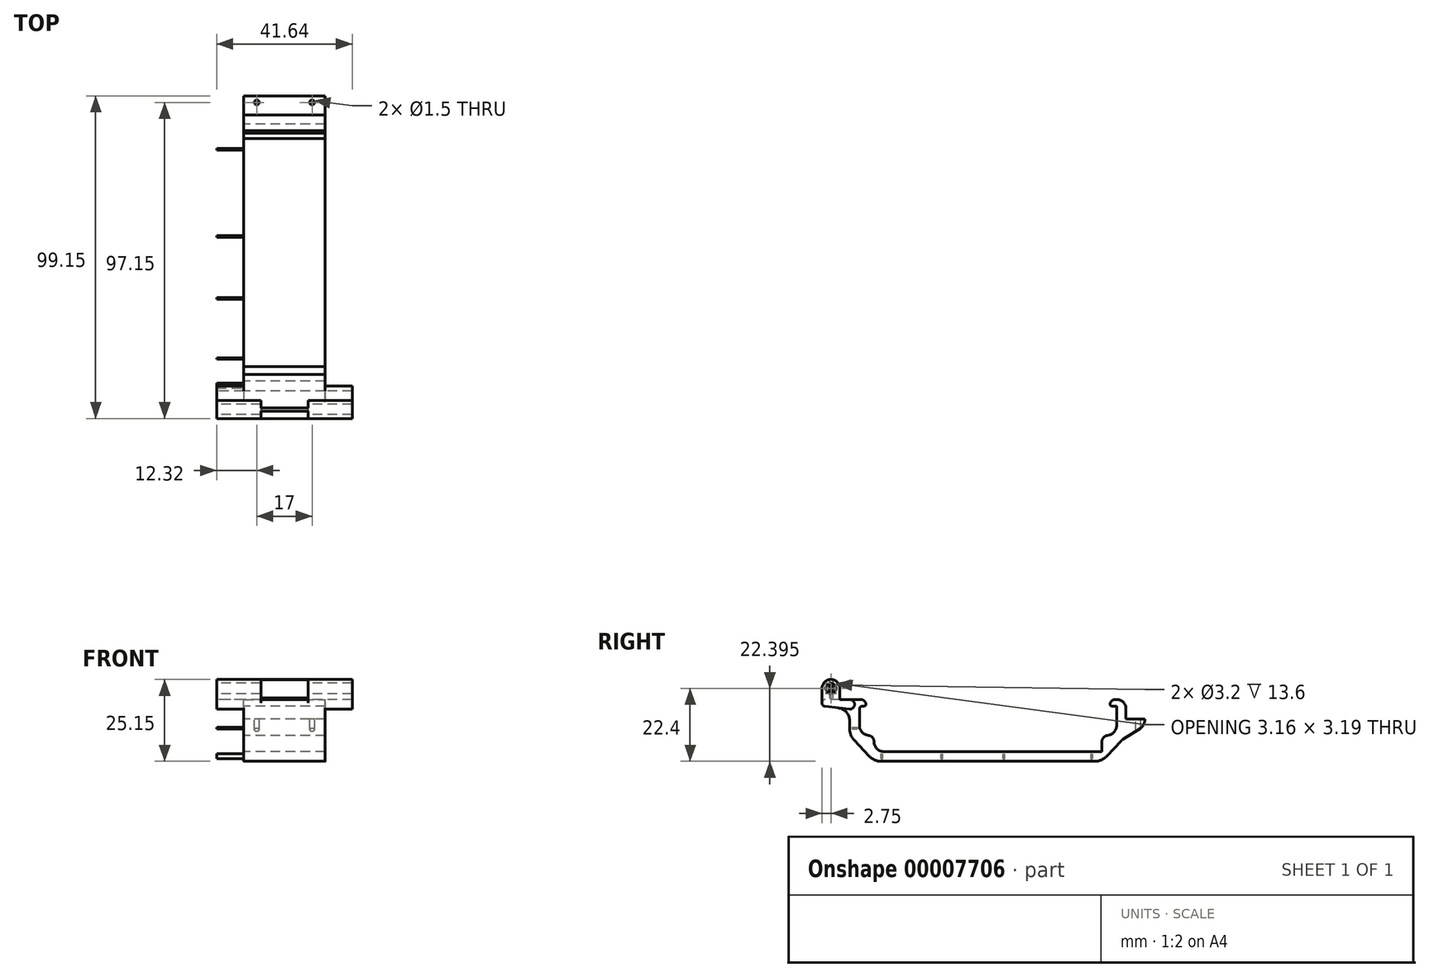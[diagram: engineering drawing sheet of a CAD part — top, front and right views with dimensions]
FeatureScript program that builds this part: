
annotation { "Feature Type Name" : "Feature", "Feature Type Description" : "" }
export const myFeature = defineFeature(function(context is Context, id is Id, definition is map)
    precondition{}
    {
        {
            var Q0;
            Q0=qCreatedBy(makeId("Right.planeOp"),FACE);
            var sketch = newSketch(context, id + "F0", { "sketchPlane" : qUnion([Q0])});
            skLineSegment(sketch, "E0.bottom", {"start": v(-38.5, 0) * mm, "end": v(-38, 0) * mm});
            skLineSegment(sketch, "E0.left", {"start": v(-39.5, -1) * mm, "end": v(-39.5, -6) * mm});
            skLineSegment(sketch, "E0.right", {"start": v(39.5, 0) * mm, "end": v(39.5, -9) * mm});
            skLineSegment(sketch, "E1.bottom", {"start": v(-35, -9) * mm, "end": v(35, -9) * mm});
            skLineSegment(sketch, "E1.top", {"start": v(-32, -14) * mm, "end": v(35, -14) * mm});
            skLineSegment(sketch, "E1.left", {"start": v(-35, -11) * mm, "end": v(-35, -11) * mm});
            skLineSegment(sketch, "E1.right", {"start": v(35, -9) * mm, "end": v(35, -14) * mm});
            skLineSegment(sketch, "E2", {"start": v(0, -14) * mm, "end": v(0, 0) * mm, "construction": true});
            skLineSegment(sketch, "E3.0", {"start": v(-42.5, -1) * mm, "end": v(-42.5, -7.02) * mm});
            skLineSegment(sketch, "E4.0", {"start": v(-32.83, -17) * mm, "end": v(0, -17) * mm});
            skLineSegment(sketch, "E5", {"start": v(-41.15, -10.44) * mm, "end": v(-36.48, -15.42) * mm});
            skLineSegment(sketch, "E6", {"start": v(-37.5, 0.5) * mm, "end": v(-37.5, 2) * mm});
            skLineSegment(sketch, "E7", {"start": v(-37.5, 2) * mm, "end": v(-39.5, 2) * mm});
            skPoint(sketch, "E8.visualSharp", {"position": v(-39.5, 0) * mm});
            skArc(sketch, "E8.filletArc", {"start": v(-38.5, 0) * mm, "mid": v(-39.2, -0.3) * mm, "end": v(-39.5, -1) * mm});
            skPoint(sketch, "E9.visualSharp", {"position": v(-39.5, -9) * mm});
            skArc(sketch, "E9.filletArc", {"start": v(-39.5, -6) * mm, "mid": v(-38.62, -8.12) * mm, "end": v(-36.5, -9) * mm});
            skArc(sketch, "E10.filletArc", {"start": v(-35, -11) * mm, "mid": v(-35.59, -9.59) * mm, "end": v(-37, -9) * mm});
            skPoint(sketch, "E11.visualSharp", {"position": v(-35, -14) * mm});
            skArc(sketch, "E11.filletArc", {"start": v(-35, -11) * mm, "mid": v(-34.12, -13.12) * mm, "end": v(-32, -14) * mm});
            skPoint(sketch, "E12.visualSharp", {"position": v(-42.5, -9) * mm});
            skArc(sketch, "E12.filletArc", {"start": v(-42.5, -7.02) * mm, "mid": v(-42.15, -8.86) * mm, "end": v(-41.15, -10.44) * mm});
            skPoint(sketch, "E13.visualSharp", {"position": v(-35, -17) * mm});
            skArc(sketch, "E13.filletArc", {"start": v(-36.48, -15.42) * mm, "mid": v(-34.82, -16.59) * mm, "end": v(-32.83, -17) * mm});
            skPoint(sketch, "E14.visualSharp", {"position": v(-42.5, 2) * mm});
            skArc(sketch, "E14.filletArc", {"start": v(-39.5, 2) * mm, "mid": v(-41.62, 1.12) * mm, "end": v(-42.5, -1) * mm});
            skPoint(sketch, "E15.newPointA", {"position": v(39.5, 0) * mm});
            skPoint(sketch, "E15.newPointB", {"position": v(-37.5, 0) * mm});
            skArc(sketch, "E15.filletArc", {"start": v(-38, 0) * mm, "mid": v(-37.65, 0.15) * mm, "end": v(-37.5, 0.5) * mm});
            skLineSegment(sketch, "E16.MirrorCS", {"start": v(37.5, 2) * mm, "end": v(39.5, 2) * mm});
            skLineSegment(sketch, "E17.MirrorCS", {"start": v(37.5, 0.5) * mm, "end": v(37.5, 2) * mm});
            skArc(sketch, "E18.MirrorCS", {"start": v(38, 0) * mm, "mid": v(37.65, 0.15) * mm, "end": v(37.5, 0.5) * mm});
            skLineSegment(sketch, "E19.MirrorCS", {"start": v(38.5, 0) * mm, "end": v(38, 0) * mm});
            skArc(sketch, "E20.MirrorCS", {"start": v(38.5, 0) * mm, "mid": v(39.2, -0.3) * mm, "end": v(39.5, -1) * mm});
            skLineSegment(sketch, "E21.MirrorCS", {"start": v(39.5, -1) * mm, "end": v(39.5, -6) * mm});
            skArc(sketch, "E22.MirrorCS", {"start": v(39.5, 2) * mm, "mid": v(41.62, 1.12) * mm, "end": v(42.5, -1) * mm});
            skLineSegment(sketch, "E23.MirrorCS", {"start": v(42.5, -1) * mm, "end": v(42.5, -7.02) * mm});
            skArc(sketch, "E24.MirrorCS", {"start": v(42.5, -7.02) * mm, "mid": v(42.15, -8.86) * mm, "end": v(41.15, -10.44) * mm});
            skLineSegment(sketch, "E25.MirrorCS", {"start": v(41.15, -10.44) * mm, "end": v(36.48, -15.42) * mm});
            skArc(sketch, "E26.MirrorCS", {"start": v(36.48, -15.42) * mm, "mid": v(34.82, -16.59) * mm, "end": v(32.83, -17) * mm});
            skLineSegment(sketch, "E27.MirrorCS", {"start": v(32.83, -17) * mm, "end": v(0, -17) * mm});
            skArc(sketch, "E28.MirrorCS", {"start": v(35, -11) * mm, "mid": v(34.12, -13.12) * mm, "end": v(32, -14) * mm});
            skArc(sketch, "E29.MirrorCS", {"start": v(35, -11) * mm, "mid": v(35.59, -9.59) * mm, "end": v(37, -9) * mm});
            skArc(sketch, "E30.MirrorCS", {"start": v(39.5, -6) * mm, "mid": v(38.62, -8.12) * mm, "end": v(36.5, -9) * mm});
            skLineSegment(sketch, "E31", {"start": v(36.68, -9.03) * mm, "end": v(37.1, -8.94) * mm});
            skLineSegment(sketch, "E32", {"start": v(-36.61, -9.04) * mm, "end": v(-37.1, -8.94) * mm});
            skLineSegment(sketch, "E33", {"start": v(51, 0) * mm, "end": v(-51, 0) * mm});
            skLineSegment(sketch, "E34.0", {"start": v(51, 2.65) * mm, "end": v(-51, 2.65) * mm});
            skCircle(sketch, "E35", {"center": v(-48.25, 2.75) * mm, "radius": 2.65 * mm, "construction": true});
            skLineSegment(sketch, "E36.bottom", {"start": v(44.15, 3) * mm, "end": v(48.15, 3) * mm});
            skLineSegment(sketch, "E36.top", {"start": v(44.15, 0) * mm, "end": v(48.15, 0) * mm});
            skLineSegment(sketch, "E36.left", {"start": v(44.15, 3) * mm, "end": v(44.15, 0) * mm});
            skLineSegment(sketch, "E36.right", {"start": v(48.15, 3) * mm, "end": v(48.15, 0) * mm});
            skLineSegment(sketch, "E37", {"start": v(51, 2.65) * mm, "end": v(51, 0) * mm});
            skLineSegment(sketch, "E38", {"start": v(-51, 0) * mm, "end": v(-42.5, -1) * mm});
            skLineSegment(sketch, "E39", {"start": v(-39.5, 2) * mm, "end": v(-53.6, 2) * mm});
            skLineSegment(sketch, "E40", {"start": v(39.5, 2) * mm, "end": v(44.15, 2) * mm});
            skCircle(sketch, "E41", {"center": v(-48.35, 2.65) * mm, "radius": 1.45 * mm, "construction": true});
            skLineSegment(sketch, "E42", {"start": v(-42.5, 2) * mm, "end": v(-42.5, -1) * mm, "construction": true});
            skArc(sketch, "E43", {"start": v(-42.85, -0.96) * mm, "mid": v(-41.5, 1.62) * mm, "end": v(-43.91, 0) * mm});
            skLineSegment(sketch, "E44", {"start": v(44.15, 2) * mm, "end": v(51, 2) * mm});
            skLineSegment(sketch, "E45", {"start": v(48.15, 0) * mm, "end": v(48.15, -6) * mm});
            skCircle(sketch, "E46", {"center": v(-48.25, 5.4) * mm, "radius": 2.75 * mm});
            skCircle(sketch, "E47", {"center": v(-48.25, 5.4) * mm, "radius": 1.6 * mm});
            skLineSegment(sketch, "E48", {"start": v(-51, 0) * mm, "end": v(-51, 5.4) * mm});
            skLineSegment(sketch, "E49", {"start": v(-45.5, 2) * mm, "end": v(-45.5, 5.4) * mm});
            skLineSegment(sketch, "E50", {"start": v(44.15, 0) * mm, "end": v(44.15, -8.54) * mm});
            skLineSegment(sketch, "E51", {"start": v(41.15, -10.44) * mm, "end": v(48.15, -6) * mm});
            skSolve(sketch);
        }
        {
            var Q0;
            {var subQ8=sQuery(id+"F0.wireOp",EDGE,"E0.left");Q0=makeQuery(id+"F0.imprint","IMPRINT",FACE,{"disambiguationData":[TD([[makeQuery(id+"F0.imprint","IMPRINT",EDGE,{"derivedFrom":subQ8}),-1.0]])]});}
            var Q1;
            {var subQ3=sQuery(id+"F0.wireOp",EDGE,"E16.MirrorCS");Q1=makeQuery(id+"F0.imprint","IMPRINT",FACE,{"disambiguationData":[TD([[makeQuery(id+"F0.imprint","IMPRINT",EDGE,{"derivedFrom":subQ3}),-1.0]])]});}
            var Q2;
            {var subQ4=sQuery(id+"F0.wireOp",EDGE,"E0.bottom");Q2=makeQuery(id+"F0.imprint","IMPRINT",FACE,{"disambiguationData":[TD([[makeQuery(id+"F0.imprint","IMPRINT",EDGE,{"derivedFrom":subQ4}),1.0]])]});}
            var Q3;
            {var subQ0=sQuery(id+"F0.wireOp",EDGE,"E43");var subQ1=sQuery(id+"F0.wireOp",EDGE,"E14.filletArc");var subQ2=makeQuery(id+"F0.imprint","INTERSECT",VERTEX,{"derivedFrom":[subQ1,subQ0]});Q3=makeQuery(id+"F0.imprint","IMPRINT",FACE,{"disambiguationData":[TD([[makeQuery(id+"F0.imprint","IMPRINT",EDGE,{"disambiguationData":[TD([[subQ2,-1.0]])],"derivedFrom":subQ1}),1.0]])]});}
            var Q4;
            {var subQ1=sQuery(id+"F0.wireOp",EDGE,"E14.filletArc");var subQ3=sQuery(id+"F0.wireOp",EDGE,"E33");var subQ4=makeQuery(id+"F0.imprint","INTERSECT",VERTEX,{"derivedFrom":[subQ1,subQ3]});Q4=makeQuery(id+"F0.imprint","IMPRINT",FACE,{"disambiguationData":[TD([[makeQuery(id+"F0.imprint","IMPRINT",EDGE,{"disambiguationData":[TD([[subQ4,1.0]])],"derivedFrom":subQ3}),1.0]])]});}
            var Q5;
            {var subQ0=sQuery(id+"F0.wireOp",EDGE,"E39");var subQ3=sQuery(id+"F0.wireOp",EDGE,"E43");var subQ5=makeQuery(id+"F0.imprint","INTERSECT",VERTEX,{"derivedFrom":[subQ0,subQ3]});Q5=makeQuery(id+"F0.imprint","IMPRINT",FACE,{"disambiguationData":[TD([[makeQuery(id+"F0.imprint","IMPRINT",EDGE,{"disambiguationData":[TD([[subQ5,1.0]])],"derivedFrom":subQ3}),-1.0]])]});}
            var Q6;
            {var subQ0=sQuery(id+"F0.wireOp",EDGE,"E43");var subQ1=sQuery(id+"F0.wireOp",EDGE,"E14.filletArc");var subQ2=makeQuery(id+"F0.imprint","INTERSECT",VERTEX,{"derivedFrom":[subQ1,subQ0]});Q6=makeQuery(id+"F0.imprint","IMPRINT",FACE,{"disambiguationData":[TD([[makeQuery(id+"F0.imprint","IMPRINT",EDGE,{"disambiguationData":[TD([[subQ2,-1.0]])],"derivedFrom":subQ1}),-1.0]])]});}
            var Q7;
            {var subQ3=sQuery(id+"F0.wireOp",EDGE,"E43");var subQ5=sQuery(id+"F0.wireOp",EDGE,"E33");var subQ6=makeQuery(id+"F0.imprint","INTERSECT",VERTEX,{"disambiguationData":[OD(0.0)],"derivedFrom":[subQ5,subQ3]});Q7=makeQuery(id+"F0.imprint","IMPRINT",FACE,{"disambiguationData":[TD([[makeQuery(id+"F0.imprint","IMPRINT",EDGE,{"disambiguationData":[TD([[subQ6,-1.0]])],"derivedFrom":subQ5}),1.0]])]});}
            var Q8;
            {var subQ4=sQuery(id+"F0.wireOp",EDGE,"ue2dPaGK-Ie0L-X2Up-9sbi-YMYjDMFNOoKe");Q8=makeQuery(id+"F0.imprint","IMPRINT",FACE,{"disambiguationData":[TD([[makeQuery(id+"F0.imprint","IMPRINT",EDGE,{"derivedFrom":subQ4}),1.0]])]});}
            var Q9;
            {var subQ0=sQuery(id+"F0.wireOp",EDGE,"E20.MirrorCS");Q9=makeQuery(id+"F0.imprint","IMPRINT",FACE,{"disambiguationData":[TD([[makeQuery(id+"F0.imprint","IMPRINT",EDGE,{"derivedFrom":subQ0}),1.0]])]});}
            var Q10;
            {var subQ4=sQuery(id+"F0.wireOp",EDGE,"E45");Q10=makeQuery(id+"F0.imprint","IMPRINT",FACE,{"disambiguationData":[TD([[makeQuery(id+"F0.imprint","IMPRINT",EDGE,{"derivedFrom":subQ4}),-1.0]])]});}
            var Q11;
            {var subQ3=sQuery(id+"F0.wireOp",EDGE,"E28.MirrorCS");Q11=makeQuery(id+"F0.imprint","IMPRINT",FACE,{"disambiguationData":[TD([[makeQuery(id+"F0.imprint","IMPRINT",EDGE,{"derivedFrom":subQ3}),1.0]])]});}
            var Q12;
            {var subQ3=sQuery(id+"F0.wireOp",EDGE,"E39");var subQ8=makeQuery(id+"F0.imprint","INTERSECT",VERTEX,{"derivedFrom":[subQ3,sQuery(id+"F0.wireOp",EDGE,"E49")]});Q12=makeQuery(id+"F0.imprint","IMPRINT",FACE,{"disambiguationData":[TD([[makeQuery(id+"F0.imprint","IMPRINT",EDGE,{"disambiguationData":[TD([[subQ8,-1.0]])],"derivedFrom":subQ3}),1.0]])]});}
            var Q13;
            {var subQ5=sQuery(id+"F0.wireOp",EDGE,"E23.MirrorCS");Q13=makeQuery(id+"F0.imprint","IMPRINT",FACE,{"disambiguationData":[TD([[makeQuery(id+"F0.imprint","IMPRINT",EDGE,{"derivedFrom":subQ5}),1.0]])]});}
            extrude(context, id + "F1", {"entities" : qUnion([Q0, Q1, Q2, Q3, Q4, Q5, Q6, Q7, Q8, Q9, Q10, Q11, Q12, Q13]), "depth" : 25 * mm, "offsetDistance" : 25 * mm});
        }
        {
            var Q0;
            {var subQ0=sQuery(id+"F0.wireOp",EDGE,"E43");var subQ1=sQuery(id+"F0.wireOp",EDGE,"E33");var subQ2=makeQuery(id+"F0.imprint","INTERSECT",VERTEX,{"disambiguationData":[OD(0.0)],"derivedFrom":[subQ1,subQ0]});Q0=makeQuery(id+"F0.imprint","IMPRINT",FACE,{"disambiguationData":[TD([[makeQuery(id+"F0.imprint","IMPRINT",EDGE,{"disambiguationData":[TD([[subQ2,-1.0]])],"derivedFrom":subQ1}),-1.0]])]});}
            var Q1;
            {var subQ3=sQuery(id+"F0.wireOp",EDGE,"E43");var subQ5=sQuery(id+"F0.wireOp",EDGE,"E33");var subQ6=makeQuery(id+"F0.imprint","INTERSECT",VERTEX,{"disambiguationData":[OD(0.0)],"derivedFrom":[subQ5,subQ3]});Q1=makeQuery(id+"F0.imprint","IMPRINT",FACE,{"disambiguationData":[TD([[makeQuery(id+"F0.imprint","IMPRINT",EDGE,{"disambiguationData":[TD([[subQ6,-1.0]])],"derivedFrom":subQ5}),1.0]])]});}
            var Q2;
            {var subQ0=sQuery(id+"F0.wireOp",EDGE,"E43");var subQ1=sQuery(id+"F0.wireOp",EDGE,"E14.filletArc");var subQ2=makeQuery(id+"F0.imprint","INTERSECT",VERTEX,{"derivedFrom":[subQ1,subQ0]});Q2=makeQuery(id+"F0.imprint","IMPRINT",FACE,{"disambiguationData":[TD([[makeQuery(id+"F0.imprint","IMPRINT",EDGE,{"disambiguationData":[TD([[subQ2,-1.0]])],"derivedFrom":subQ1}),-1.0]])]});}
            var Q3;
            {var subQ0=sQuery(id+"F0.wireOp",EDGE,"E43");var subQ1=sQuery(id+"F0.wireOp",EDGE,"E14.filletArc");var subQ2=makeQuery(id+"F0.imprint","INTERSECT",VERTEX,{"derivedFrom":[subQ1,subQ0]});Q3=makeQuery(id+"F0.imprint","IMPRINT",FACE,{"disambiguationData":[TD([[makeQuery(id+"F0.imprint","IMPRINT",EDGE,{"disambiguationData":[TD([[subQ2,-1.0]])],"derivedFrom":subQ1}),1.0]])]});}
            var Q4;
            {var subQ1=sQuery(id+"F0.wireOp",EDGE,"E14.filletArc");var subQ3=sQuery(id+"F0.wireOp",EDGE,"E33");var subQ4=makeQuery(id+"F0.imprint","INTERSECT",VERTEX,{"derivedFrom":[subQ1,subQ3]});Q4=makeQuery(id+"F0.imprint","IMPRINT",FACE,{"disambiguationData":[TD([[makeQuery(id+"F0.imprint","IMPRINT",EDGE,{"disambiguationData":[TD([[subQ4,1.0]])],"derivedFrom":subQ3}),1.0]])]});}
            extrude(context, id + "F2", {"entities" : qUnion([Q0, Q1, Q2, Q3, Q4]), "operationType" : NewBodyOperationType.ADD, "depth" : 33.31 * mm, "offsetDistance" : 25 * mm, "hasSecondDirection" : true, "secondDirectionOppositeDirection" : true, "secondDirectionDepth" : 8.3 * mm});
        }
        {
            var Q0;
            {var subQ0=sQuery(id+"F0.wireOp",EDGE,"E46");var subQ1=sQuery(id+"F0.wireOp",EDGE,"E34.0");var subQ2=makeQuery(id+"F0.imprint","INTERSECT",VERTEX,{"derivedFrom":[subQ1,subQ0]});Q0=makeQuery(id+"F0.imprint","IMPRINT",FACE,{"disambiguationData":[TD([[makeQuery(id+"F0.imprint","IMPRINT",EDGE,{"disambiguationData":[TD([[subQ2,1.0]])],"derivedFrom":subQ1}),-1.0]])]});}
            var Q1;
            Q1=makeQuery(id+"F0.imprint","IMPRINT",FACE,{"disambiguationData":[TD([[makeQuery(id+"F0.imprint","IMPRINT",EDGE,{"derivedFrom":sQuery(id+"F0.wireOp",EDGE,"E47")}),-1.0]])]});
            var Q2;
            {var subQ0=sQuery(id+"F0.wireOp",EDGE,"E46");var subQ1=sQuery(id+"F0.wireOp",EDGE,"E34.0");var subQ2=makeQuery(id+"F0.imprint","INTERSECT",VERTEX,{"derivedFrom":[subQ1,subQ0]});Q2=makeQuery(id+"F0.imprint","IMPRINT",FACE,{"disambiguationData":[TD([[makeQuery(id+"F0.imprint","IMPRINT",EDGE,{"disambiguationData":[TD([[subQ2,-1.0]])],"derivedFrom":subQ1}),-1.0]])]});}
            var Q3;
            {var subQ1=sQuery(id+"F0.wireOp",EDGE,"E34.0");var subQ7=makeQuery(id+"F0.imprint","INTERSECT",VERTEX,{"derivedFrom":[subQ1,sQuery(id+"F0.wireOp",EDGE,"E46")]});Q3=makeQuery(id+"F0.imprint","IMPRINT",FACE,{"disambiguationData":[TD([[makeQuery(id+"F0.imprint","IMPRINT",EDGE,{"disambiguationData":[TD([[subQ7,-1.0]])],"derivedFrom":subQ1}),1.0]])]});}
            extrude(context, id + "F3", {"entities" : qUnion([Q0, Q1, Q2, Q3]), "operationType" : NewBodyOperationType.ADD, "depth" : 5.3 * mm, "offsetDistance" : 25 * mm, "hasSecondDirection" : true, "secondDirectionOppositeDirection" : true, "secondDirectionDepth" : 8.3 * mm});
        }
        {
            var Q0;
            {var subQ1=sQuery(id+"F0.wireOp",EDGE,"E34.0");var subQ7=makeQuery(id+"F0.imprint","INTERSECT",VERTEX,{"derivedFrom":[subQ1,sQuery(id+"F0.wireOp",EDGE,"E46")]});Q0=makeQuery(id+"F0.imprint","IMPRINT",FACE,{"disambiguationData":[TD([[makeQuery(id+"F0.imprint","IMPRINT",EDGE,{"disambiguationData":[TD([[subQ7,-1.0]])],"derivedFrom":subQ1}),1.0]])]});}
            var Q1;
            {var subQ0=sQuery(id+"F0.wireOp",EDGE,"E46");var subQ1=sQuery(id+"F0.wireOp",EDGE,"E34.0");var subQ2=makeQuery(id+"F0.imprint","INTERSECT",VERTEX,{"derivedFrom":[subQ1,subQ0]});Q1=makeQuery(id+"F0.imprint","IMPRINT",FACE,{"disambiguationData":[TD([[makeQuery(id+"F0.imprint","IMPRINT",EDGE,{"disambiguationData":[TD([[subQ2,1.0]])],"derivedFrom":subQ1}),-1.0]])]});}
            var Q2;
            {var subQ0=sQuery(id+"F0.wireOp",EDGE,"E46");var subQ1=sQuery(id+"F0.wireOp",EDGE,"E34.0");var subQ2=makeQuery(id+"F0.imprint","INTERSECT",VERTEX,{"derivedFrom":[subQ1,subQ0]});Q2=makeQuery(id+"F0.imprint","IMPRINT",FACE,{"disambiguationData":[TD([[makeQuery(id+"F0.imprint","IMPRINT",EDGE,{"disambiguationData":[TD([[subQ2,-1.0]])],"derivedFrom":subQ1}),-1.0]])]});}
            var Q3;
            Q3=makeQuery(id+"F0.imprint","IMPRINT",FACE,{"disambiguationData":[TD([[makeQuery(id+"F0.imprint","IMPRINT",EDGE,{"derivedFrom":sQuery(id+"F0.wireOp",EDGE,"E47")}),-1.0]])]});
            extrude(context, id + "F4", {"entities" : qUnion([Q0, Q1, Q2, Q3]), "operationType" : NewBodyOperationType.ADD, "depth" : 33.31 * mm, "offsetDistance" : 25 * mm, "hasSecondDirection" : true, "secondDirectionOppositeDirection" : false, "secondDirectionDepth" : 19.71 * mm});
        }
        {
            var Q0;
            Q0=makeQuery(id+"F1.opExtrude","SWEPT_FACE",FACE,{"disambiguationData":[OSD([sQuery(id+"F0.wireOp",EDGE,"E33")])]});
            var sketch = newSketch(context, id + "F5", { "sketchPlane" : qUnion([Q0])});
            skLineSegment(sketch, "E52", {"start": v(12.5, 48.15) * mm, "end": v(12.5, 37.5) * mm, "construction": true});
            skLineSegment(sketch, "E53.0", {"start": v(25, 44.15) * mm, "end": v(0, 44.15) * mm});
            skLineSegment(sketch, "E54.0", {"start": v(2, 48.15) * mm, "end": v(2, 37.5) * mm});
            skLineSegment(sketch, "E55.0", {"start": v(23, 48.15) * mm, "end": v(23, 37.5) * mm});
            skLineSegment(sketch, "E56", {"start": v(4, 44.15) * mm, "end": v(4, 48.15) * mm, "construction": true});
            skLineSegment(sketch, "E57", {"start": v(21, 44.15) * mm, "end": v(21, 48.15) * mm, "construction": true});
            skCircle(sketch, "E58", {"center": v(21, 46.15) * mm, "radius": 0.75 * mm});
            skCircle(sketch, "E59", {"center": v(4, 46.15) * mm, "radius": 0.75 * mm});
            skSolve(sketch);
        }
        {
            var Q0;
            Q0 = qSketchRegion(id + "F5", true);
            var Q1;
            Q1=makeQuery(id+"F1.opExtrude","SWEPT_FACE",FACE,{"disambiguationData":[OSD([sQuery(id+"F0.wireOp",EDGE,"E33")])]});
            extrude(context, id + "F6", {"entities" : qUnion([Q0, Q1]), "operationType" : NewBodyOperationType.REMOVE, "oppositeDirection" : true, "depth" : 4 * mm, "offsetDistance" : 25 * mm});
        }
        {
            var Q0;
            Q0=makeQuery(id+"F5.imprint","IMPRINT",FACE,{"disambiguationData":[TD([[makeQuery(id+"F5.imprint","IMPRINT",EDGE,{"derivedFrom":sQuery(id+"F5.wireOp",EDGE,"E58")}),1.0]])]});
            var Q1;
            Q1=makeQuery(id+"F5.imprint","IMPRINT",FACE,{"disambiguationData":[TD([[makeQuery(id+"F5.imprint","IMPRINT",EDGE,{"derivedFrom":sQuery(id+"F5.wireOp",EDGE,"E59")}),1.0]])]});
            extrude(context, id + "F7", {"entities" : qUnion([Q0, Q1]), "operationType" : NewBodyOperationType.REMOVE, "oppositeDirection" : true, "depth" : 25 * mm, "offsetDistance" : 25 * mm});
        }
        {
            var Q0;
            Q0=makeQuery(id+"F1.opExtrude","SWEPT_EDGE",EDGE,{"disambiguationData":[OSD([sQuery(id+"F0.wireOp",EDGE,"E6"),sQuery(id+"F0.wireOp",EDGE,"E7")])]});
            var Q1;
            Q1=makeQuery(id+"FMFm3wJr4hb81Ca_1.boolean.opBoolean","COPY",EDGE,{"derivedFrom":makeQuery(id+"FMFm3wJr4hb81Ca_1.opExtrude","CAP_EDGE",EDGE,{"disambiguationData":[OSD([sQuery(id+"F5.wireOp",EDGE,"ea55a457-8957-4b89-8185-e320d8a5e55b.0")])],"isStart":false})});
            var Q2;
            Q2=makeQuery(id+"F1.opExtrude","SWEPT_EDGE",EDGE,{"disambiguationData":[OSD([sQuery(id+"F0.wireOp",EDGE,"E16.MirrorCS"),sQuery(id+"F0.wireOp",EDGE,"E17.MirrorCS")])]});
            var Q3;
            Q3=makeQuery(id+"FMFm3wJr4hb81Ca_1.boolean.opBoolean","COPY",EDGE,{"derivedFrom":makeQuery(id+"FMFm3wJr4hb81Ca_1.opExtrude","CAP_EDGE",EDGE,{"disambiguationData":[OSD([sQuery(id+"F5.wireOp",EDGE,"ea55a457-8957-4b89-8185-e320d8a5e55b.0")])],"isStart":true})});
            chamfer(context, id + "F8", {"entities" : qUnion([Q0, Q1, Q2, Q3]), "width" : 1 * mm, "tangentPropagation" : true});
        }
        {
            var Q0;
            {var subQ0=sQuery(id+"F5.wireOp",EDGE,"ea55a457-8957-4b89-8185-e320d8a5e55b.0");Q0=makeQuery(id+"F8.opChamfer","BLEND_EDGE",EDGE,{"blendedFrom":[makeQuery(id+"FMFm3wJr4hb81Ca_1.boolean.opBoolean","COPY",EDGE,{"derivedFrom":makeQuery(id+"FMFm3wJr4hb81Ca_1.opExtrude","CAP_EDGE",EDGE,{"disambiguationData":[OSD([subQ0])],"isStart":false})}),makeQuery(id+"FMFm3wJr4hb81Ca_1.boolean.opBoolean","COPY",FACE,{"derivedFrom":makeQuery(id+"FMFm3wJr4hb81Ca_1.opExtrude","CAP_FACE",FACE,{"disambiguationData":[OSD([sQuery(id+"F0.wireOp",EDGE,"E16.MirrorCS"),sQuery(id+"F0.wireOp",EDGE,"E36.right"),sQuery(id+"F0.wireOp",EDGE,"E40"),sQuery(id+"F0.wireOp",EDGE,"E44"),sQuery(id+"F5.wireOp",EDGE,"E53.0"),sQuery(id+"F5.wireOp",EDGE,"E54.0"),sQuery(id+"F5.wireOp",EDGE,"E55.0"),subQ0])],"isStart":false})})],"blendedInto":[makeQuery(id+"FMFm3wJr4hb81Ca_1.boolean.opBoolean","COPY",FACE,{"derivedFrom":makeQuery(id+"FMFm3wJr4hb81Ca_1.opExtrude","CAP_FACE",FACE,{"disambiguationData":[OSD([sQuery(id+"F0.wireOp",EDGE,"E16.MirrorCS"),sQuery(id+"F0.wireOp",EDGE,"E36.right"),sQuery(id+"F0.wireOp",EDGE,"E40"),sQuery(id+"F0.wireOp",EDGE,"E44"),sQuery(id+"F5.wireOp",EDGE,"E53.0"),sQuery(id+"F5.wireOp",EDGE,"E54.0"),sQuery(id+"F5.wireOp",EDGE,"E55.0"),subQ0])],"isStart":false})})]});}
            var Q1;
            {var subQ2=sQuery(id+"F0.wireOp",EDGE,"E44");var subQ5=sQuery(id+"F0.wireOp",EDGE,"E40");var subQ21=sQuery(id+"F0.wireOp",EDGE,"E17.MirrorCS");var subQ22=sQuery(id+"F0.wireOp",EDGE,"E16.MirrorCS");var subQ40=sQuery(id+"F5.wireOp",EDGE,"ea55a457-8957-4b89-8185-e320d8a5e55b.0");Q1=makeQuery(id+"F8.opChamfer","BLEND_EDGE",EDGE,{"blendedFrom":[makeQuery(id+"FMFm3wJr4hb81Ca_1.boolean.opBoolean","COPY",EDGE,{"derivedFrom":makeQuery(id+"FMFm3wJr4hb81Ca_1.opExtrude","CAP_EDGE",EDGE,{"disambiguationData":[OSD([subQ40])],"isStart":true})}),makeQuery(id+"FMFm3wJr4hb81Ca_1.boolean.opBoolean","SPLIT",FACE,{"disambiguationData":[TD([makeQuery(id+"F1.opExtrude","SWEPT_FACE",FACE,{"disambiguationData":[OSD([subQ21])]})])],"derivedFrom":makeQuery(id+"F1.opExtrude","SWEPT_FACE",FACE,{"disambiguationData":[OSD([subQ22,subQ5,subQ2])]})})],"blendedInto":[makeQuery(id+"FMFm3wJr4hb81Ca_1.boolean.opBoolean","SPLIT",FACE,{"disambiguationData":[TD([makeQuery(id+"F1.opExtrude","SWEPT_FACE",FACE,{"disambiguationData":[OSD([subQ21])]})])],"derivedFrom":makeQuery(id+"F1.opExtrude","SWEPT_FACE",FACE,{"disambiguationData":[OSD([subQ22,subQ5,subQ2])]})})]});}
            var Q2;
            {var subQ2=sQuery(id+"F0.wireOp",EDGE,"E44");var subQ5=sQuery(id+"F0.wireOp",EDGE,"E40");var subQ21=sQuery(id+"F0.wireOp",EDGE,"E17.MirrorCS");var subQ22=sQuery(id+"F0.wireOp",EDGE,"E16.MirrorCS");Q2=makeQuery(id+"F8.opChamfer","BLEND_EDGE",EDGE,{"blendedFrom":[makeQuery(id+"F1.opExtrude","SWEPT_EDGE",EDGE,{"disambiguationData":[OSD([subQ22,subQ21])]}),makeQuery(id+"FMFm3wJr4hb81Ca_1.boolean.opBoolean","SPLIT",FACE,{"disambiguationData":[TD([makeQuery(id+"F1.opExtrude","SWEPT_FACE",FACE,{"disambiguationData":[OSD([subQ21])]})])],"derivedFrom":makeQuery(id+"F1.opExtrude","SWEPT_FACE",FACE,{"disambiguationData":[OSD([subQ22,subQ5,subQ2])]})})],"blendedInto":[makeQuery(id+"FMFm3wJr4hb81Ca_1.boolean.opBoolean","SPLIT",FACE,{"disambiguationData":[TD([makeQuery(id+"F1.opExtrude","SWEPT_FACE",FACE,{"disambiguationData":[OSD([subQ21])]})])],"derivedFrom":makeQuery(id+"F1.opExtrude","SWEPT_FACE",FACE,{"disambiguationData":[OSD([subQ22,subQ5,subQ2])]})})]});}
            var Q3;
            {var subQ0=sQuery(id+"F0.wireOp",EDGE,"E17.MirrorCS");Q3=makeQuery(id+"F8.opChamfer","BLEND_EDGE",EDGE,{"blendedFrom":[makeQuery(id+"F1.opExtrude","SWEPT_EDGE",EDGE,{"disambiguationData":[OSD([sQuery(id+"F0.wireOp",EDGE,"E16.MirrorCS"),subQ0])]}),makeQuery(id+"F1.opExtrude","SWEPT_FACE",FACE,{"disambiguationData":[OSD([subQ0])]})],"blendedInto":[makeQuery(id+"F1.opExtrude","SWEPT_FACE",FACE,{"disambiguationData":[OSD([subQ0])]})]});}
            var Q4;
            {var subQ0=sQuery(id+"F0.wireOp",EDGE,"E39");var subQ1=sQuery(id+"F0.wireOp",EDGE,"E7");Q4=makeQuery(id+"F8.opChamfer","BLEND_EDGE",EDGE,{"blendedFrom":[makeQuery(id+"F1.opExtrude","SWEPT_EDGE",EDGE,{"disambiguationData":[OSD([sQuery(id+"F0.wireOp",EDGE,"E6"),subQ1])]}),makeQuery(id+"F2.boolean.opBoolean","MERGE",FACE,{"derivedFrom":[makeQuery(id+"F1.opExtrude","SWEPT_FACE",FACE,{"disambiguationData":[OSD([subQ1,subQ0])]}),makeQuery(id+"F2.opExtrude","SWEPT_FACE",FACE,{"disambiguationData":[OSD([subQ0])]})]})],"blendedInto":[makeQuery(id+"F2.boolean.opBoolean","MERGE",FACE,{"derivedFrom":[makeQuery(id+"F1.opExtrude","SWEPT_FACE",FACE,{"disambiguationData":[OSD([subQ1,subQ0])]}),makeQuery(id+"F2.opExtrude","SWEPT_FACE",FACE,{"disambiguationData":[OSD([subQ0])]})]})]});}
            var Q5;
            {var subQ0=sQuery(id+"F0.wireOp",EDGE,"E6");Q5=makeQuery(id+"F8.opChamfer","BLEND_EDGE",EDGE,{"blendedFrom":[makeQuery(id+"F1.opExtrude","SWEPT_EDGE",EDGE,{"disambiguationData":[OSD([subQ0,sQuery(id+"F0.wireOp",EDGE,"E7")])]}),makeQuery(id+"F1.opExtrude","SWEPT_FACE",FACE,{"disambiguationData":[OSD([subQ0])]})],"blendedInto":[makeQuery(id+"F1.opExtrude","SWEPT_FACE",FACE,{"disambiguationData":[OSD([subQ0])]})]});}
            var Q6;
            {var subQ0=sQuery(id+"F0.wireOp",EDGE,"8w9qb6zW-Nx0w-tlVl-g2Rt-QB6cGm39T1tt");var subQ1=sQuery(id+"F0.wireOp",EDGE,"E38");Q6=makeQuery(id+"F2.boolean.opBoolean","MERGE",EDGE,{"derivedFrom":[makeQuery(id+"F1.opExtrude","SWEPT_EDGE",EDGE,{"disambiguationData":[OSD([subQ1,subQ0])]}),makeQuery(id+"F2.opExtrude","SWEPT_EDGE",EDGE,{"disambiguationData":[OSD([subQ1,subQ0])]})]});}
            var Q7;
            Q7=makeQuery(id+"F4.boolean.opBoolean","SPLIT",EDGE,{"derivedFrom":makeQuery(id+"F3.boolean.opBoolean","SPLIT",EDGE,{"derivedFrom":makeQuery(id+"F2.opExtrude","SWEPT_EDGE",EDGE,{"disambiguationData":[OSD([sQuery(id+"F0.wireOp",EDGE,"E35"),sQuery(id+"F0.wireOp",EDGE,"E39"),sQuery(id+"F0.wireOp",EDGE,"8w9qb6zW-Nx0w-tlVl-g2Rt-QB6cGm39T1tt")])]})})});
            fillet(context, id + "F9", {"entities" : qUnion([Q0, Q1, Q2, Q3, Q4, Q5, Q6, Q7]), "tangentPropagation" : true, "radius" : 1 * mm, "defaultsChanged" : false, "vertexSettings" : [], "allowEdgeOverflow" : false});
        }
        {
            var Q0;
            Q0=makeQuery(id+"F1.opExtrude","SWEPT_EDGE",EDGE,{"disambiguationData":[OSD([sQuery(id+"F0.wireOp",EDGE,"E23.MirrorCS"),sQuery(id+"F0.wireOp",EDGE,"E24.MirrorCS"),sQuery(id+"F0.wireOp",EDGE,"ppJ8474i-59gJ-vrmH-Dv7L-EUcPLqEBuoak")])]});
            var Q1;
            Q1=makeQuery(id+"F1.opExtrude","SWEPT_EDGE",EDGE,{"disambiguationData":[OSD([sQuery(id+"F0.wireOp",EDGE,"E45"),sQuery(id+"F0.wireOp",EDGE,"ppJ8474i-59gJ-vrmH-Dv7L-EUcPLqEBuoak")])]});
            fillet(context, id + "F10", {"entities" : qUnion([Q0, Q1]), "tangentPropagation" : true, "radius" : 3 * mm, "defaultsChanged" : false, "vertexSettings" : [], "allowEdgeOverflow" : false});
        }
        {
            var Q0;
            Q0=makeQuery(id+"F1.opExtrude","SWEPT_EDGE",EDGE,{"disambiguationData":[OSD([sQuery(id+"F0.wireOp",EDGE,"E3.0"),sQuery(id+"F0.wireOp",EDGE,"E14.filletArc"),sQuery(id+"F0.wireOp",EDGE,"E38"),sQuery(id+"F0.wireOp",EDGE,"E43")])]});
            fillet(context, id + "F11", {"entities" : qUnion([Q0]), "tangentPropagation" : true, "radius" : 4 * mm, "defaultsChanged" : true, "vertexSettings" : [], "allowEdgeOverflow" : false});
        }
        {
            var Q0;
            Q0=makeQuery(id+"F1.opExtrude","CAP_FACE",FACE,{"disambiguationData":[OSD([sQuery(id+"F0.wireOp",EDGE,"E0.bottom"),sQuery(id+"F0.wireOp",EDGE,"E0.left"),sQuery(id+"F0.wireOp",EDGE,"E0.right"),sQuery(id+"F0.wireOp",EDGE,"E1.top"),sQuery(id+"F0.wireOp",EDGE,"E3.0"),sQuery(id+"F0.wireOp",EDGE,"E4.0"),sQuery(id+"F0.wireOp",EDGE,"E5"),sQuery(id+"F0.wireOp",EDGE,"E6"),sQuery(id+"F0.wireOp",EDGE,"E7"),sQuery(id+"F0.wireOp",EDGE,"E8.filletArc"),sQuery(id+"F0.wireOp",EDGE,"E9.filletArc"),sQuery(id+"F0.wireOp",EDGE,"E10.filletArc"),sQuery(id+"F0.wireOp",EDGE,"E11.filletArc"),sQuery(id+"F0.wireOp",EDGE,"E12.filletArc"),sQuery(id+"F0.wireOp",EDGE,"E13.filletArc"),sQuery(id+"F0.wireOp",EDGE,"E15.filletArc"),sQuery(id+"F0.wireOp",EDGE,"E16.MirrorCS"),sQuery(id+"F0.wireOp",EDGE,"E17.MirrorCS"),sQuery(id+"F0.wireOp",EDGE,"E18.MirrorCS"),sQuery(id+"F0.wireOp",EDGE,"E19.MirrorCS"),sQuery(id+"F0.wireOp",EDGE,"E20.MirrorCS"),sQuery(id+"F0.wireOp",EDGE,"E24.MirrorCS"),sQuery(id+"F0.wireOp",EDGE,"E25.MirrorCS"),sQuery(id+"F0.wireOp",EDGE,"E26.MirrorCS"),sQuery(id+"F0.wireOp",EDGE,"E27.MirrorCS"),sQuery(id+"F0.wireOp",EDGE,"E28.MirrorCS"),sQuery(id+"F0.wireOp",EDGE,"E29.MirrorCS"),sQuery(id+"F0.wireOp",EDGE,"E30.MirrorCS"),sQuery(id+"F0.wireOp",EDGE,"E31"),sQuery(id+"F0.wireOp",EDGE,"E32"),sQuery(id+"F0.wireOp",EDGE,"E33"),sQuery(id+"F0.wireOp",EDGE,"E36.right"),sQuery(id+"F0.wireOp",EDGE,"E38"),sQuery(id+"F0.wireOp",EDGE,"E39"),sQuery(id+"F0.wireOp",EDGE,"E40"),sQuery(id+"F0.wireOp",EDGE,"8w9qb6zW-Nx0w-tlVl-g2Rt-QB6cGm39T1tt"),sQuery(id+"F0.wireOp",EDGE,"E43"),sQuery(id+"F0.wireOp",EDGE,"E44"),sQuery(id+"F0.wireOp",EDGE,"E45"),sQuery(id+"F0.wireOp",EDGE,"ppJ8474i-59gJ-vrmH-Dv7L-EUcPLqEBuoak")])],"isStart":true});
            var sketch = newSketch(context, id + "F12", { "sketchPlane" : qUnion([Q0])});
            skArc(sketch, "E60.1", {"start": v(-47.3, -4.8) * mm, "mid": v(-46.92, -5.66) * mm, "end": v(-46.2, -6.28) * mm});
            skArc(sketch, "E60.2", {"start": v(35.9, -14.87) * mm, "mid": v(34.5, -15.85) * mm, "end": v(32.83, -16.2) * mm});
            skLineSegment(sketch, "E60.3", {"start": v(40.56, -9.9) * mm, "end": v(35.9, -14.87) * mm});
            skArc(sketch, "E60.4", {"start": v(41.7, -7.02) * mm, "mid": v(41.4, -8.57) * mm, "end": v(40.56, -9.9) * mm});
            skLineSegment(sketch, "E60.5", {"start": v(41.7, -4.56) * mm, "end": v(41.7, -7.02) * mm});
            skLineSegment(sketch, "E60.6", {"start": v(32.83, -16.2) * mm, "end": v(-32.83, -16.2) * mm});
            skArc(sketch, "E60.7", {"start": v(-35.9, -14.87) * mm, "mid": v(-34.5, -15.85) * mm, "end": v(-32.83, -16.2) * mm});
            skLineSegment(sketch, "E60.8", {"start": v(-40.73, -9.72) * mm, "end": v(-35.9, -14.87) * mm});
            skLineSegment(sketch, "E60.11", {"start": v(-41.7, -9.44) * mm, "end": v(-46.2, -6.28) * mm});
            skLineSegment(sketch, "E61.2", {"start": v(-40.3, -1) * mm, "end": v(-40.3, -1) * mm});
            skLineSegment(sketch, "E61.3", {"start": v(-40.3, -1) * mm, "end": v(-40.3, -6) * mm});
            skArc(sketch, "E61.4", {"start": v(35.8, -11) * mm, "mid": v(36.07, -10.24) * mm, "end": v(36.77, -9.82) * mm});
            skLineSegment(sketch, "E61.5", {"start": v(36.77, -9.82) * mm, "end": v(37.25, -9.72) * mm});
            skArc(sketch, "E61.6", {"start": v(40.3, -6) * mm, "mid": v(39.44, -8.4) * mm, "end": v(37.25, -9.72) * mm});
            skLineSegment(sketch, "E61.7", {"start": v(40.3, -1) * mm, "end": v(40.3, -6) * mm});
            skArc(sketch, "E61.8", {"start": v(35.8, -11) * mm, "mid": v(34.69, -13.69) * mm, "end": v(32, -14.8) * mm});
            skLineSegment(sketch, "E61.9", {"start": v(32, -14.8) * mm, "end": v(-32, -14.8) * mm});
            skArc(sketch, "E61.10", {"start": v(-35.8, -11) * mm, "mid": v(-34.69, -13.69) * mm, "end": v(-32, -14.8) * mm});
            skArc(sketch, "E61.11", {"start": v(-35.8, -11) * mm, "mid": v(-36.1, -10.22) * mm, "end": v(-36.83, -9.81) * mm});
            skLineSegment(sketch, "E61.12", {"start": v(-36.83, -9.81) * mm, "end": v(-37.27, -9.72) * mm});
            skArc(sketch, "E61.13", {"start": v(-40.3, -6) * mm, "mid": v(-39.45, -8.4) * mm, "end": v(-37.27, -9.72) * mm});
            skLineSegment(sketch, "E62", {"start": v(40.3, -1) * mm, "end": v(39.6, 0.22) * mm});
            skLineSegment(sketch, "E63", {"start": v(39.6, 0.22) * mm, "end": v(38.5, 0.59) * mm});
            skPoint(sketch, "E64.visualSharp", {"position": v(37.84, 0.8) * mm});
            skLineSegment(sketch, "E65", {"start": v(41.7, -4.56) * mm, "end": v(42.5, -4.56) * mm});
            skLineSegment(sketch, "E66", {"start": v(41.7, -7.02) * mm, "end": v(40.16, -7.02) * mm});
            skLineSegment(sketch, "E67.0", {"start": v(41.7, -6.52) * mm, "end": v(40.26, -6.52) * mm});
            skLineSegment(sketch, "E68", {"start": v(32.83, -16.2) * mm, "end": v(32.83, -14.7) * mm});
            skLineSegment(sketch, "E69.0", {"start": v(32.33, -16.2) * mm, "end": v(32.33, -14.79) * mm});
            skLineSegment(sketch, "E70", {"start": v(14.4, -16.2) * mm, "end": v(14.4, -14.8) * mm});
            skLineSegment(sketch, "E71", {"start": v(-5.18, -16.2) * mm, "end": v(-5.18, -14.8) * mm});
            skLineSegment(sketch, "E72", {"start": v(-32, -14.8) * mm, "end": v(-32, -16.2) * mm});
            skLineSegment(sketch, "E73", {"start": v(-42, -9.22) * mm, "end": v(-38.52, -9.22) * mm});
            skLineSegment(sketch, "E74.0", {"start": v(-40.73, -9.72) * mm, "end": v(-37.27, -9.72) * mm});
            skLineSegment(sketch, "E75.0", {"start": v(-31.5, -14.8) * mm, "end": v(-31.5, -16.8) * mm});
            skLineSegment(sketch, "E76.0", {"start": v(-4.68, -16.2) * mm, "end": v(-4.68, -14.2) * mm});
            skLineSegment(sketch, "E77.0", {"start": v(13.9, -16.2) * mm, "end": v(13.9, -14.2) * mm});
            skLineSegment(sketch, "E78", {"start": v(38.5, 0.59) * mm, "end": v(38.91, 2) * mm});
            skLineSegment(sketch, "E79", {"start": v(-47.3, -4.8) * mm, "end": v(-41.46, -4.8) * mm});
            skLineSegment(sketch, "E80", {"start": v(-41.46, -4.8) * mm, "end": v(-41.46, 0) * mm});
            skArc(sketch, "E81.0", {"start": v(-39.5, 1.2) * mm, "mid": v(-40.65, 0.88) * mm, "end": v(-41.46, 0) * mm});
            skLineSegment(sketch, "E81.1", {"start": v(-38.91, 1.2) * mm, "end": v(-39.5, 1.2) * mm});
            skArc(sketch, "E81.2", {"start": v(-38.77, 1.14) * mm, "mid": v(-38.84, 1.18) * mm, "end": v(-38.91, 1.2) * mm});
            skLineSegment(sketch, "E81.3", {"start": v(-38.43, 0.8) * mm, "end": v(-38.77, 1.14) * mm});
            skArc(sketch, "E81.4", {"start": v(-38.5, 0.8) * mm, "mid": v(-39.77, 0.27) * mm, "end": v(-40.3, -1) * mm});
            skLineSegment(sketch, "E81.5", {"start": v(-38.5, 0.8) * mm, "end": v(-38.43, 0.8) * mm});
            skSolve(sketch);
        }
        {
            var Q0;
            Q0=makeQuery(id+"F12.imprint","IMPRINT",FACE,{"disambiguationData":[TD([[makeQuery(id+"F12.imprint","IMPRINT",EDGE,{"derivedFrom":sQuery(id+"F12.wireOp",EDGE,"E60.0")}),-1.0]])]});
            var Q1;
            {var subQ0=sQuery(id+"F12.wireOp",EDGE,"E73");Q1=makeQuery(id+"F12.imprint","IMPRINT",FACE,{"disambiguationData":[TD([[makeQuery(id+"F12.imprint","IMPRINT",EDGE,{"derivedFrom":subQ0}),-1.0]])]});}
            var Q2;
            {var subQ0=sQuery(id+"F12.wireOp",EDGE,"E72");Q2=makeQuery(id+"F12.imprint","IMPRINT",FACE,{"disambiguationData":[TD([[makeQuery(id+"F12.imprint","IMPRINT",EDGE,{"derivedFrom":subQ0}),1.0]])]});}
            var Q3;
            {var subQ0=sQuery(id+"F12.wireOp",EDGE,"E71");Q3=makeQuery(id+"F12.imprint","IMPRINT",FACE,{"disambiguationData":[TD([[makeQuery(id+"F12.imprint","IMPRINT",EDGE,{"derivedFrom":subQ0}),-1.0]])]});}
            var Q4;
            {var subQ0=sQuery(id+"F12.wireOp",EDGE,"E70");Q4=makeQuery(id+"F12.imprint","IMPRINT",FACE,{"disambiguationData":[TD([[makeQuery(id+"F12.imprint","IMPRINT",EDGE,{"derivedFrom":subQ0}),1.0]])]});}
            var Q5;
            {var subQ0=sQuery(id+"F12.wireOp",EDGE,"E68");Q5=makeQuery(id+"F12.imprint","IMPRINT",FACE,{"disambiguationData":[TD([[makeQuery(id+"F12.imprint","IMPRINT",EDGE,{"derivedFrom":subQ0}),1.0]])]});}
            var Q6;
            {var subQ0=sQuery(id+"F12.wireOp",EDGE,"E66");Q6=makeQuery(id+"F12.imprint","IMPRINT",FACE,{"disambiguationData":[TD([[makeQuery(id+"F12.imprint","IMPRINT",EDGE,{"derivedFrom":subQ0}),-1.0]])]});}
            var Q7;
            {var subQ0=sQuery(id+"F0.wireOp",EDGE,"E48");var subQ1=sQuery(id+"F0.wireOp",EDGE,"E39");Q7=makeQuery(id+"F3.boolean.opBoolean","MERGE",FACE,{"derivedFrom":[makeQuery(id+"F2.opExtrude","CAP_FACE",FACE,{"disambiguationData":[OSD([sQuery(id+"F0.wireOp",EDGE,"E38"),subQ1,sQuery(id+"F0.wireOp",EDGE,"E43"),subQ0])],"isStart":true}),makeQuery(id+"F3.opExtrude","CAP_FACE",FACE,{"disambiguationData":[OSD([subQ1,sQuery(id+"F0.wireOp",EDGE,"E46"),sQuery(id+"F0.wireOp",EDGE,"E47"),subQ0,sQuery(id+"F0.wireOp",EDGE,"E49")])],"isStart":true})]});}
            extrude(context, id + "F13", {"entities" : qUnion([Q0, Q1, Q2, Q3, Q4, Q5, Q6]), "operationType" : NewBodyOperationType.ADD, "endBound" : BoundingType.UP_TO_SURFACE, "depth" : 25 * mm, "endBoundEntityFace" : qUnion([Q7]), "offsetDistance" : 25 * mm});
        }
        {
            var Q0;
            Q0=makeQuery(id+"F4.opExtrude","CAP_FACE",FACE,{"disambiguationData":[OSD([sQuery(id+"F0.wireOp",EDGE,"E39"),sQuery(id+"F0.wireOp",EDGE,"E46"),sQuery(id+"F0.wireOp",EDGE,"E47"),sQuery(id+"F0.wireOp",EDGE,"E48"),sQuery(id+"F0.wireOp",EDGE,"E49")])],"isStart":true});
            var sketch = newSketch(context, id + "F14", { "sketchPlane" : qUnion([Q0])});
            skLineSegment(sketch, "E82", {"start": v(47.75, 2) * mm, "end": v(47.75, 8.1) * mm});
            skLineSegment(sketch, "E83.0", {"start": v(48.75, 2) * mm, "end": v(48.75, 8.1) * mm});
            skLineSegment(sketch, "E84.0", {"start": v(45.7, 2.5) * mm, "end": v(50, 2.5) * mm});
            skSolve(sketch);
        }
        {
            var Q0;
            {var subQ0=sQuery(id+"F14.wireOp",EDGE,"E82");var subQ1=makeQuery(id+"F4.opExtrude","CAP_EDGE",EDGE,{"disambiguationData":[OSD([sQuery(id+"F0.wireOp",EDGE,"E47")])],"isStart":true});var subQ2=makeQuery(id+"F14.imprint","INTERSECT",VERTEX,{"disambiguationData":[OD(0.0)],"derivedFrom":[subQ1,subQ0]});Q0=makeQuery(id+"F14.imprint","IMPRINT",FACE,{"disambiguationData":[TD([[makeQuery(id+"F14.imprint","IMPRINT",EDGE,{"disambiguationData":[TD([[subQ2,-1.0]])],"derivedFrom":subQ0}),-1.0]])]});}
            var Q1;
            {var subQ0=sQuery(id+"F14.wireOp",EDGE,"E82");var subQ1=makeQuery(id+"F4.opExtrude","CAP_EDGE",EDGE,{"disambiguationData":[OSD([sQuery(id+"F0.wireOp",EDGE,"E46")])],"isStart":true});var subQ2=makeQuery(id+"F14.imprint","INTERSECT",VERTEX,{"derivedFrom":[subQ1,subQ0]});Q1=makeQuery(id+"F14.imprint","IMPRINT",FACE,{"disambiguationData":[TD([[makeQuery(id+"F14.imprint","IMPRINT",EDGE,{"disambiguationData":[TD([[subQ2,1.0]])],"derivedFrom":subQ0}),-1.0]])]});}
            var Q2;
            {var subQ0=sQuery(id+"F14.wireOp",EDGE,"E84.0");var subQ1=sQuery(id+"F14.wireOp",EDGE,"E82");var subQ2=makeQuery(id+"F14.imprint","INTERSECT",VERTEX,{"derivedFrom":[subQ1,subQ0]});Q2=makeQuery(id+"F14.imprint","IMPRINT",FACE,{"disambiguationData":[TD([[makeQuery(id+"F14.imprint","IMPRINT",EDGE,{"disambiguationData":[TD([[subQ2,-1.0]])],"derivedFrom":subQ1}),-1.0]])]});}
            var Q3;
            Q3=makeQuery(id+"F3.opExtrude","CAP_FACE",FACE,{"disambiguationData":[OSD([sQuery(id+"F0.wireOp",EDGE,"E39"),sQuery(id+"F0.wireOp",EDGE,"E46"),sQuery(id+"F0.wireOp",EDGE,"E47"),sQuery(id+"F0.wireOp",EDGE,"E48"),sQuery(id+"F0.wireOp",EDGE,"E49")])],"isStart":false});
            extrude(context, id + "F15", {"entities" : qUnion([Q0, Q1, Q2]), "operationType" : NewBodyOperationType.ADD, "endBound" : BoundingType.UP_TO_SURFACE, "depth" : 25 * mm, "endBoundEntityFace" : qUnion([Q3]), "offsetDistance" : 25 * mm});
        }
    });
